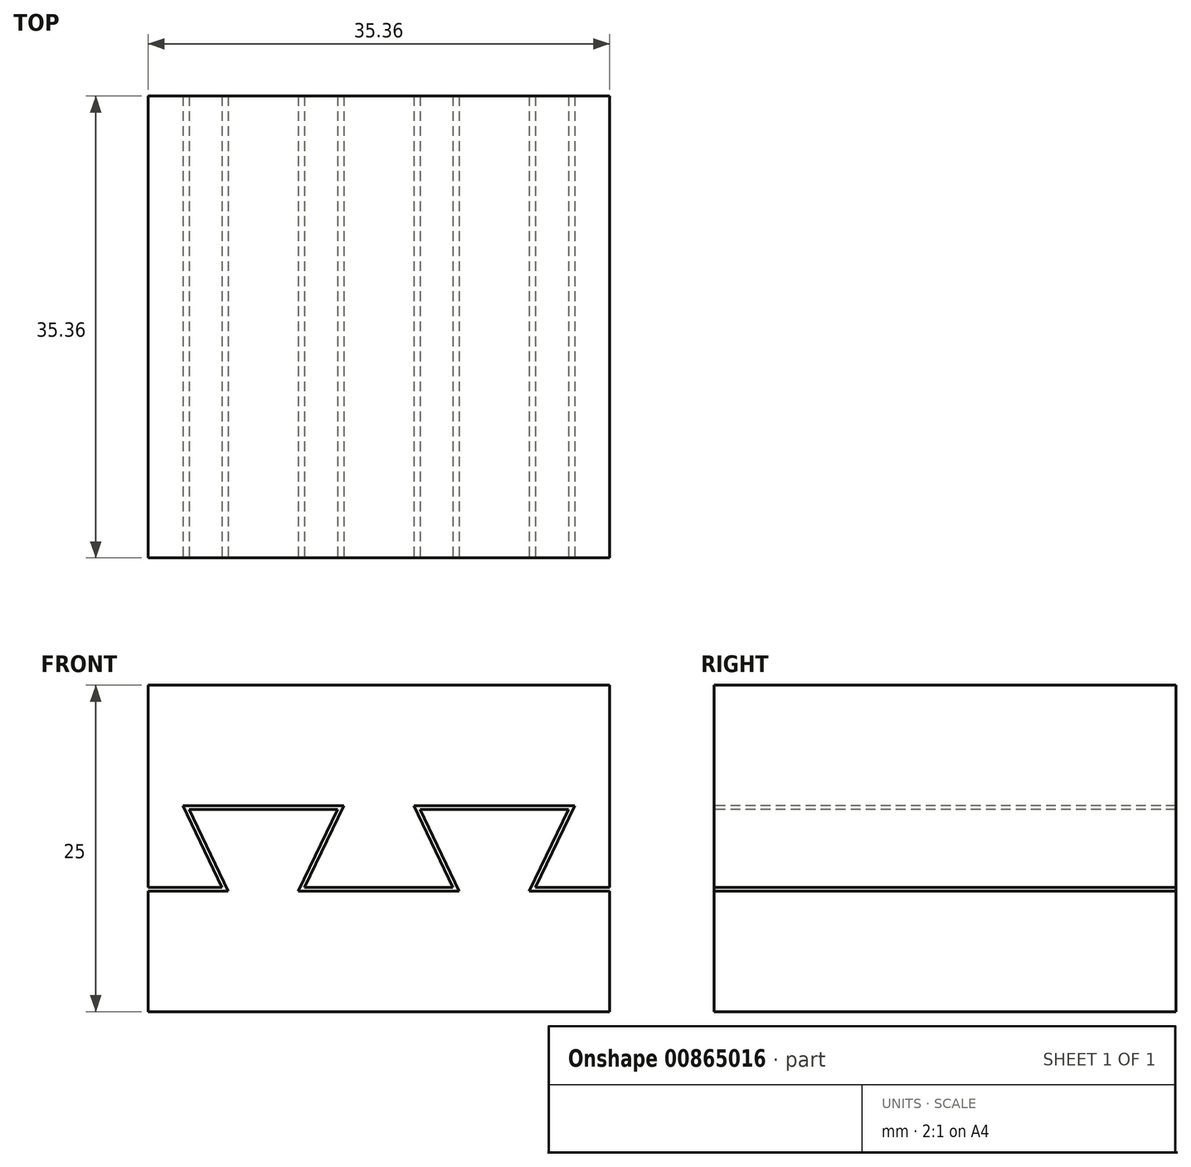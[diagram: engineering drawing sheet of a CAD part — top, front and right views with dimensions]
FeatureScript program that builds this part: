
annotation { "Feature Type Name" : "Feature", "Feature Type Description" : "" }
export const myFeature = defineFeature(function(context is Context, id is Id, definition is map)
    precondition{}
    {
        {
            var Q0;
            Q0=qCreatedBy(makeId("Top.planeOp"),FACE);
            var sketch = newSketch(context, id + "F0", { "sketchPlane" : qUnion([Q0])});
            skLineSegment(sketch, "E0.bottom", {"start": v(0, 0) * mm, "end": v(35.36, 0) * mm});
            skLineSegment(sketch, "E0.top", {"start": v(0, -35.36) * mm, "end": v(35.36, -35.36) * mm});
            skLineSegment(sketch, "E0.left", {"start": v(0, 0) * mm, "end": v(0, -35.36) * mm});
            skLineSegment(sketch, "E0.right", {"start": v(35.36, 0) * mm, "end": v(35.36, -35.36) * mm});
            skSolve(sketch);
        }
        {
            var Q0;
            Q0=makeQuery(id+"F0.imprint","IMPRINT",FACE,{"disambiguationData":[TD([[makeQuery(id+"F0.imprint","IMPRINT",EDGE,{"derivedFrom":sQuery(id+"F0.wireOp",EDGE,"E0.bottom")}),-1.0]])]});
            extrude(context, id + "F1", {"entities" : qUnion([Q0]), "depth" : 25 * mm, "offsetDistance" : 25 * mm});
        }
        {
            var Q0;
            Q0=makeQuery(id+"F1.opExtrude","SWEPT_FACE",FACE,{"disambiguationData":[OSD([sQuery(id+"F0.wireOp",EDGE,"E0.top")])]});
            var sketch = newSketch(context, id + "F2", { "sketchPlane" : qUnion([Q0])});
            skLineSegment(sketch, "E1", {"start": v(0, 9.38) * mm, "end": v(5.92, 9.38) * mm, "construction": true});
            skLineSegment(sketch, "E2", {"start": v(2.92, 15.63) * mm, "end": v(5.92, 9.38) * mm, "construction": true});
            skLineSegment(sketch, "E3", {"start": v(2.92, 15.62) * mm, "end": v(8.84, 15.62) * mm, "construction": true});
            skLineSegment(sketch, "E4", {"start": v(8.84, 15.62) * mm, "end": v(14.76, 15.62) * mm, "construction": true});
            skLineSegment(sketch, "E5", {"start": v(14.76, 15.62) * mm, "end": v(11.76, 9.37) * mm, "construction": true});
            skLineSegment(sketch, "E6", {"start": v(11.76, 9.38) * mm, "end": v(17.68, 9.38) * mm, "construction": true});
            skLineSegment(sketch, "E7", {"start": v(17.68, 9.38) * mm, "end": v(23.6, 9.38) * mm, "construction": true});
            skLineSegment(sketch, "E8", {"start": v(20.6, 15.63) * mm, "end": v(23.6, 9.37) * mm, "construction": true});
            skLineSegment(sketch, "E9", {"start": v(20.6, 15.62) * mm, "end": v(26.52, 15.62) * mm, "construction": true});
            skLineSegment(sketch, "E10", {"start": v(26.52, 15.62) * mm, "end": v(32.44, 15.62) * mm, "construction": true});
            skLineSegment(sketch, "E11", {"start": v(32.44, 15.62) * mm, "end": v(29.44, 9.37) * mm, "construction": true});
            skLineSegment(sketch, "E12", {"start": v(29.44, 9.38) * mm, "end": v(35.36, 9.38) * mm, "construction": true});
            skLineSegment(sketch, "E13", {"start": v(20.6, 15.63) * mm, "end": v(20.6, 12.5) * mm, "construction": true});
            skLineSegment(sketch, "E14", {"start": v(20.6, 12.5) * mm, "end": v(20.6, 9.38) * mm, "construction": true});
            skLineSegment(sketch, "E15", {"start": v(35.36, 9.38) * mm, "end": v(35.36, 12.5) * mm});
            skLineSegment(sketch, "E16", {"start": v(14.76, 15.63) * mm, "end": v(14.76, 9.38) * mm, "construction": true});
            skLineSegment(sketch, "E17", {"start": v(20.6, 9.38) * mm, "end": v(23.6, 9.38) * mm, "construction": true});
            skLineSegment(sketch, "E18", {"start": v(14.76, 9.38) * mm, "end": v(11.76, 9.38) * mm, "construction": true});
            skLineSegment(sketch, "E19.0", {"start": v(32.67, 15.77) * mm, "end": v(29.67, 9.52) * mm});
            skLineSegment(sketch, "E20.trimOffspring", {"start": v(29.67, 9.53) * mm, "end": v(35.36, 9.53) * mm});
            skLineSegment(sketch, "E21.0", {"start": v(32.67, 15.78) * mm, "end": v(32.67, 15.78) * mm});
            skLineSegment(sketch, "E21.1", {"start": v(20.36, 15.78) * mm, "end": v(32.67, 15.78) * mm});
            skLineSegment(sketch, "E21.2", {"start": v(20.36, 15.78) * mm, "end": v(23.36, 9.52) * mm});
            skLineSegment(sketch, "E22.0", {"start": v(12, 9.53) * mm, "end": v(23.36, 9.53) * mm});
            skLineSegment(sketch, "E22.1", {"start": v(12, 9.53) * mm, "end": v(12, 9.53) * mm});
            skLineSegment(sketch, "E22.2", {"start": v(15, 15.77) * mm, "end": v(12, 9.52) * mm});
            skLineSegment(sketch, "E22.3", {"start": v(0, 9.53) * mm, "end": v(5.68, 9.53) * mm});
            skLineSegment(sketch, "E22.4", {"start": v(2.68, 15.78) * mm, "end": v(5.68, 9.53) * mm});
            skLineSegment(sketch, "E22.5", {"start": v(2.68, 15.78) * mm, "end": v(15, 15.78) * mm});
            skLineSegment(sketch, "E22.6", {"start": v(15, 15.78) * mm, "end": v(15, 15.78) * mm});
            skLineSegment(sketch, "E23.0", {"start": v(0, 25) * mm, "end": v(35.36, 25) * mm});
            skLineSegment(sketch, "E23.1", {"start": v(35.36, 25) * mm, "end": v(35.36, 0) * mm});
            skLineSegment(sketch, "E23.2", {"start": v(0, 0) * mm, "end": v(35.36, 0) * mm});
            skLineSegment(sketch, "E23.3", {"start": v(0, 25) * mm, "end": v(0, 0) * mm});
            skLineSegment(sketch, "E24.0", {"start": v(29.2, 9.22) * mm, "end": v(35.36, 9.22) * mm});
            skLineSegment(sketch, "E24.1", {"start": v(32.2, 15.47) * mm, "end": v(29.2, 9.22) * mm});
            skLineSegment(sketch, "E24.2", {"start": v(8.84, 15.47) * mm, "end": v(14.52, 15.47) * mm});
            skLineSegment(sketch, "E24.3", {"start": v(3.16, 15.47) * mm, "end": v(8.84, 15.47) * mm});
            skLineSegment(sketch, "E24.4", {"start": v(3.16, 15.48) * mm, "end": v(6.16, 9.23) * mm});
            skLineSegment(sketch, "E24.5", {"start": v(0, 9.22) * mm, "end": v(6.16, 9.22) * mm});
            skLineSegment(sketch, "E24.6", {"start": v(14.52, 15.47) * mm, "end": v(11.52, 9.22) * mm});
            skLineSegment(sketch, "E24.7", {"start": v(11.52, 9.22) * mm, "end": v(17.68, 9.22) * mm});
            skLineSegment(sketch, "E24.8", {"start": v(17.68, 9.22) * mm, "end": v(23.84, 9.22) * mm});
            skLineSegment(sketch, "E24.9", {"start": v(20.84, 15.47) * mm, "end": v(23.84, 9.22) * mm});
            skLineSegment(sketch, "E24.10", {"start": v(20.84, 15.47) * mm, "end": v(26.52, 15.47) * mm});
            skLineSegment(sketch, "E24.11", {"start": v(26.52, 15.47) * mm, "end": v(32.2, 15.47) * mm});
            skSolve(sketch);
        }
        {
            var Q0;
            Q0=makeQuery(id+"F2.imprint","IMPRINT",FACE,{"disambiguationData":[TD([[makeQuery(id+"F2.imprint","IMPRINT",EDGE,{"derivedFrom":sQuery(id+"F2.wireOp",EDGE,"E19.0")}),-1.0]])]});
            var Q1;
            Q1=makeQuery(id+"F1.opExtrude","SWEPT_FACE",FACE,{"disambiguationData":[OSD([sQuery(id+"F0.wireOp",EDGE,"E0.bottom")])]});
            extrude(context, id + "F3", {"entities" : qUnion([Q0]), "operationType" : NewBodyOperationType.REMOVE, "endBound" : BoundingType.UP_TO_SURFACE, "oppositeDirection" : true, "depth" : 25 * mm, "endBoundEntityFace" : qUnion([Q1]), "offsetDistance" : 25 * mm});
        }
    });
